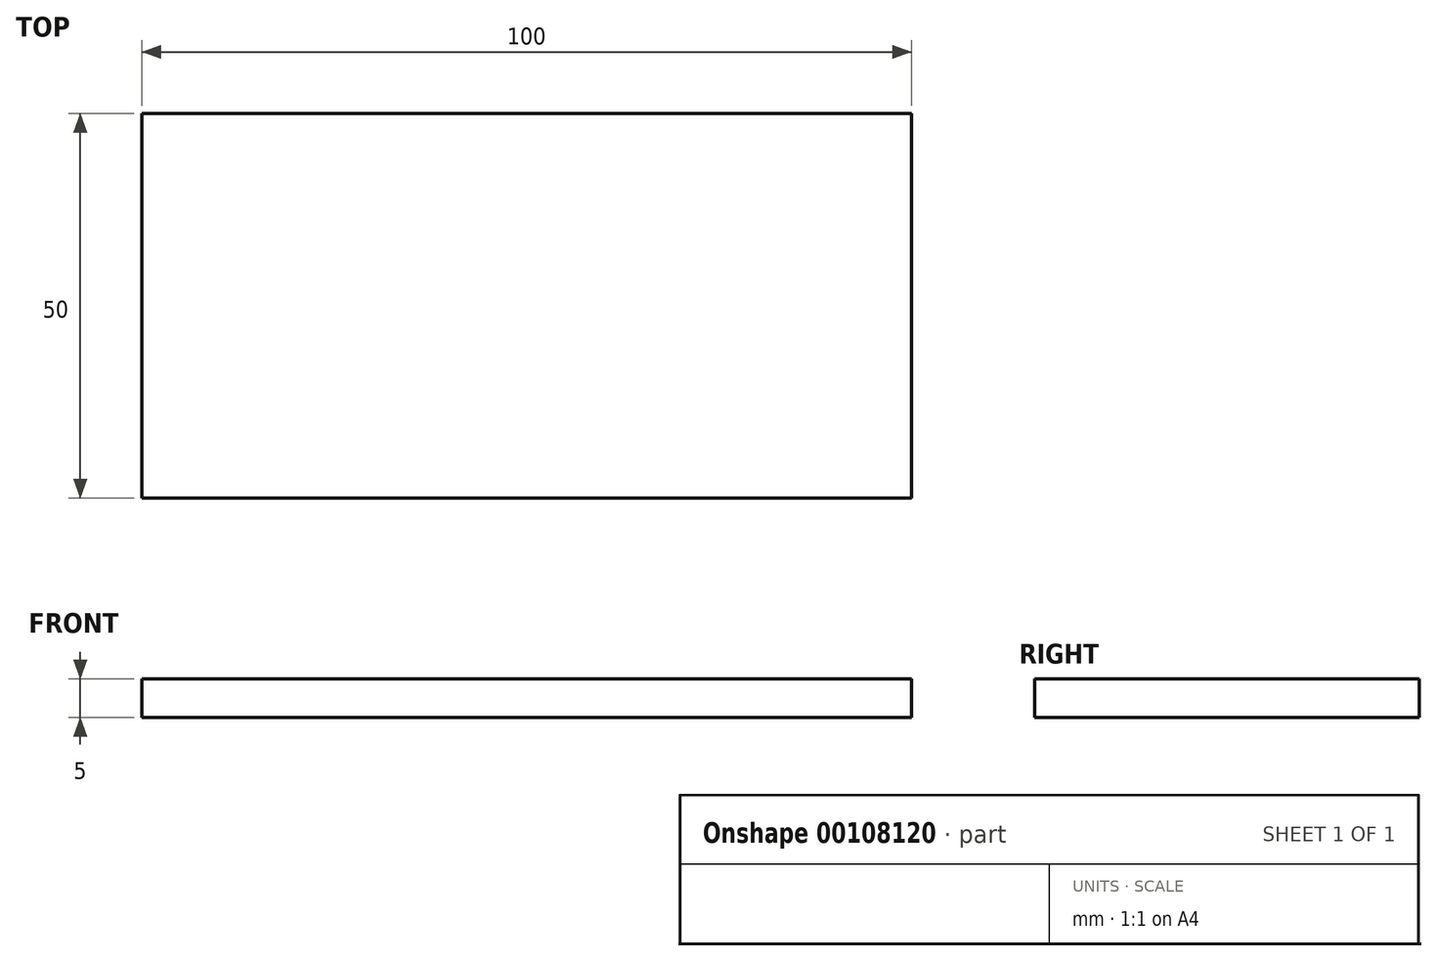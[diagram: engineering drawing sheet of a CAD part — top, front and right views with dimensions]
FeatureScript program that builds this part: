
annotation { "Feature Type Name" : "Feature", "Feature Type Description" : "" }
export const myFeature = defineFeature(function(context is Context, id is Id, definition is map)
    precondition{}
    {
        {
            var Q0;
            Q0=qCreatedBy(makeId("Top.planeOp"),FACE);
            var sketch = newSketch(context, id + "F0", { "sketchPlane" : qUnion([Q0])});
            skLineSegment(sketch, "E0.bottom", {"start": v(50, -25) * mm, "end": v(-50, -25) * mm});
            skLineSegment(sketch, "E0.top", {"start": v(50, 25) * mm, "end": v(-50, 25) * mm});
            skLineSegment(sketch, "E0.left", {"start": v(50, -25) * mm, "end": v(50, 25) * mm});
            skLineSegment(sketch, "E0.right", {"start": v(-50, -25) * mm, "end": v(-50, 25) * mm});
            skPoint(sketch, "E0.middle", {"position": v(0, 0) * mm});
            skSolve(sketch);
        }
        {
            var Q0;
            Q0=makeQuery(id+"F0.imprint","IMPRINT",FACE,{"disambiguationData":[TD([[makeQuery(id+"F0.imprint","IMPRINT",EDGE,{"derivedFrom":sQuery(id+"F0.wireOp",EDGE,"E0.bottom")}),-1.0]])]});
            extrude(context, id + "F1", {"entities" : qUnion([Q0]), "depth" : 5 * mm});
        }
    });
